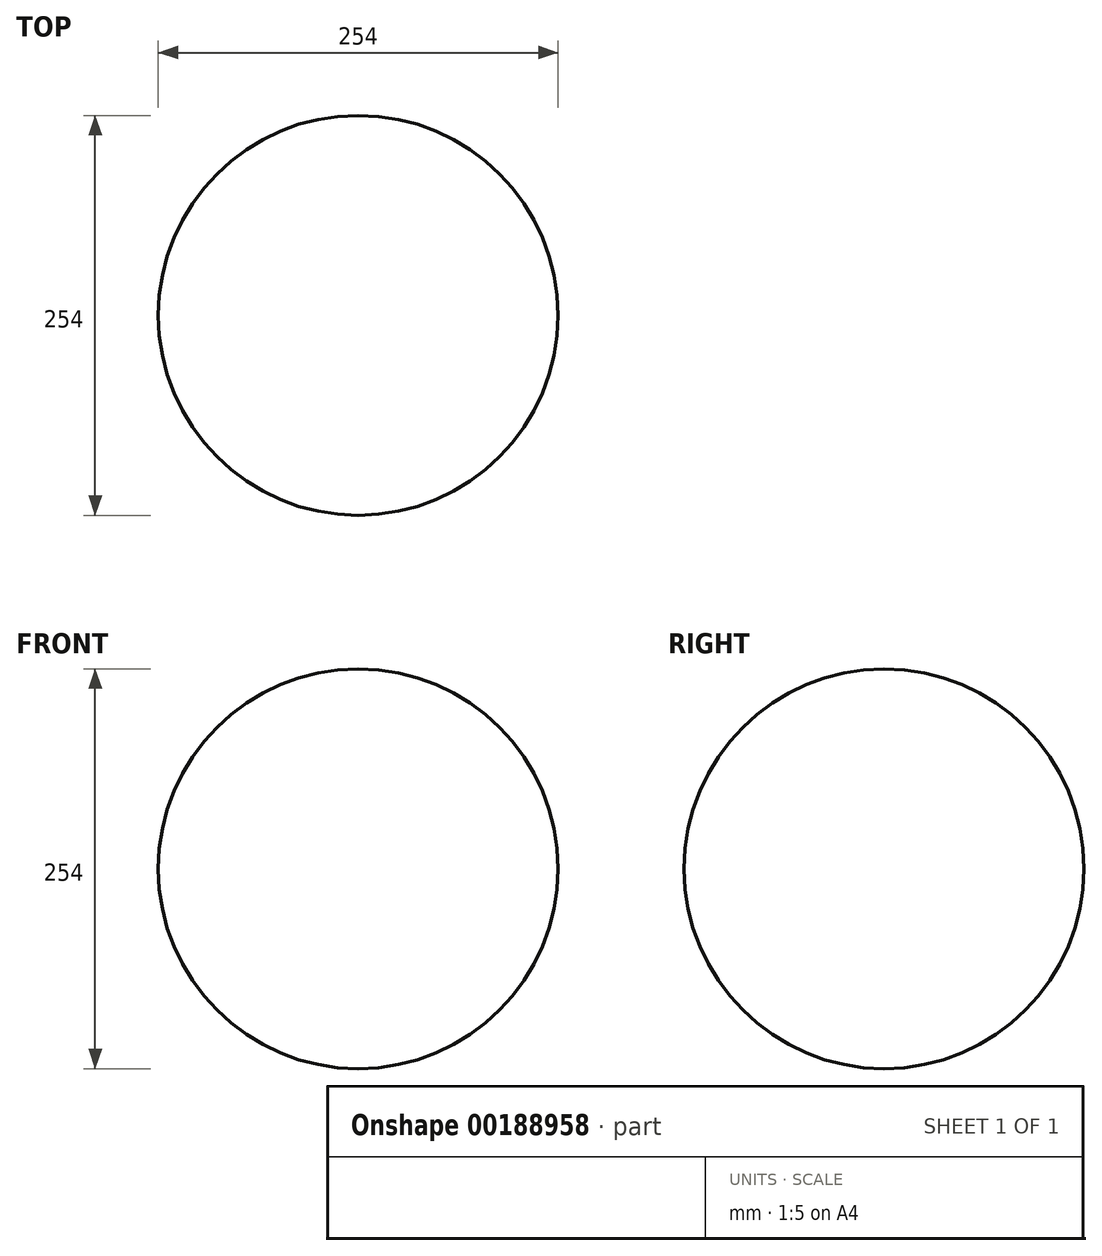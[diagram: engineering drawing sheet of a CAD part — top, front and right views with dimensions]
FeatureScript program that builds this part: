
annotation { "Feature Type Name" : "Feature", "Feature Type Description" : "" }
export const myFeature = defineFeature(function(context is Context, id is Id, definition is map)
    precondition{}
    {
        {
            var Q0;
            Q0=qCreatedBy(makeId("Top.planeOp"),FACE);
            var sketch = newSketch(context, id + "F0", { "sketchPlane" : qUnion([Q0])});
            skArc(sketch, "E0", {"start": v(91.97, 24.44) * mm, "mid": v(-35.03, 151.44) * mm, "end": v(-162.03, 24.44) * mm});
            skLineSegment(sketch, "E1", {"start": v(91.97, 24.44) * mm, "end": v(-162.03, 24.44) * mm});
            skLineSegment(sketch, "E2", {"start": v(-35.03, 24.44) * mm, "end": v(-35.03, 151.44) * mm, "construction": true});
            skSolve(sketch);
        }
        {
            var Q0;
            Q0=makeQuery(id+"F0.imprint","IMPRINT",FACE,{"disambiguationData":[TD([[makeQuery(id+"F0.imprint","IMPRINT",EDGE,{"derivedFrom":sQuery(id+"F0.wireOp",EDGE,"E0")}),1.0]])]});
            var Q1;
            Q1=sQuery(id+"F0.wireOp",EDGE,"E1");
            revolve(context, id + "F1", {"entities" : qUnion([Q0]), "axis" : qUnion([Q1]), "revolveType" : RevolveType.FULL});
        }
    });
